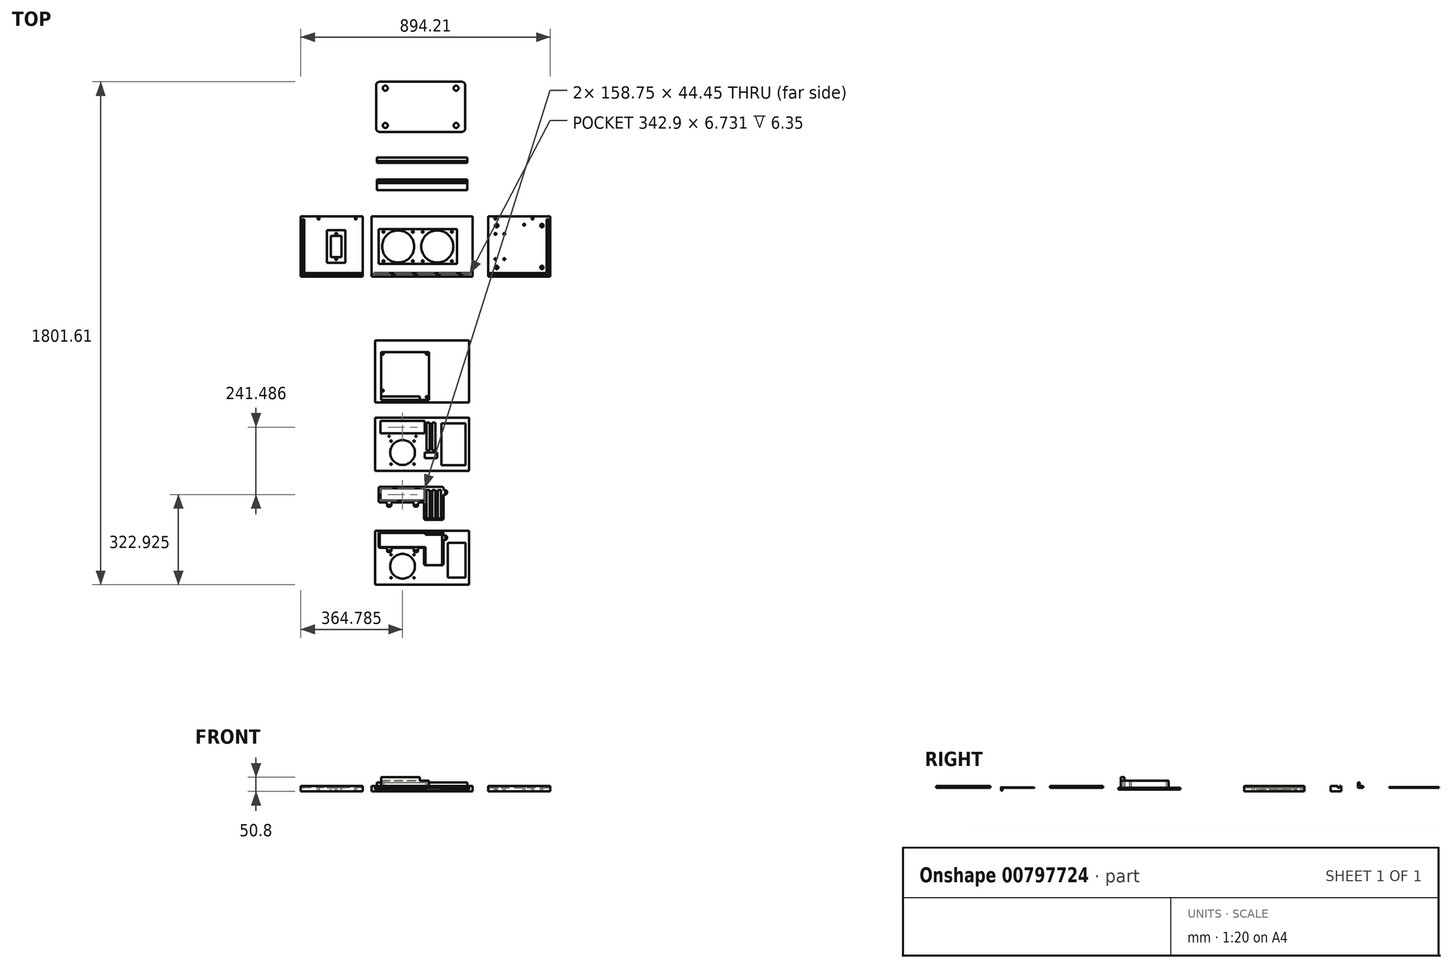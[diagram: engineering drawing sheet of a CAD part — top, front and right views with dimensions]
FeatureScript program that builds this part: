
annotation { "Feature Type Name" : "Feature", "Feature Type Description" : "" }
export const myFeature = defineFeature(function(context is Context, id is Id, definition is map)
    precondition{}
    {
        {
            var Q0;
            Q0=qCreatedBy(makeId("Top.planeOp"),FACE);
            var sketch = newSketch(context, id + "F0", { "sketchPlane" : qUnion([Q0])});
            skLineSegment(sketch, "E0.bottom", {"start": v(120.65, -107.95) * mm, "end": v(-241.3, -107.95) * mm});
            skLineSegment(sketch, "E0.top", {"start": v(120.65, 107.95) * mm, "end": v(-241.3, 107.95) * mm});
            skLineSegment(sketch, "E0.left", {"start": v(120.65, -107.95) * mm, "end": v(120.65, 107.95) * mm});
            skLineSegment(sketch, "E0.right", {"start": v(-241.3, -107.95) * mm, "end": v(-241.3, 107.95) * mm});
            skLineSegment(sketch, "E1.bottom", {"start": v(-231.77, -101.6) * mm, "end": v(111.12, -101.6) * mm});
            skLineSegment(sketch, "E1.top", {"start": v(-231.77, -94.87) * mm, "end": v(111.12, -94.87) * mm});
            skLineSegment(sketch, "E1.left", {"start": v(-231.77, -101.6) * mm, "end": v(-231.77, -94.87) * mm});
            skLineSegment(sketch, "E1.right", {"start": v(111.12, -101.6) * mm, "end": v(111.12, -94.87) * mm});
            skPoint(sketch, "E2.middle", {"position": v(-145.7, 0) * mm});
            skCircle(sketch, "E3", {"center": v(-145.7, 0) * mm, "radius": 57.5 * mm});
            skCircle(sketch, "E4", {"center": v(-198.2, 52.5) * mm, "radius": 3.3 * mm});
            skCircle(sketch, "E5", {"center": v(-93.2, 52.5) * mm, "radius": 3.3 * mm});
            skCircle(sketch, "E6", {"center": v(-198.2, -52.5) * mm, "radius": 3.3 * mm});
            skCircle(sketch, "E7", {"center": v(-93.2, -52.5) * mm, "radius": 3.3 * mm});
            skPoint(sketch, "E8.middle", {"position": v(-5.3, 0) * mm});
            skCircle(sketch, "E9", {"center": v(-5.3, 0) * mm, "radius": 57.5 * mm});
            skCircle(sketch, "E10", {"center": v(-57.8, 52.5) * mm, "radius": 3.3 * mm});
            skCircle(sketch, "E11", {"center": v(47.2, 52.5) * mm, "radius": 3.3 * mm});
            skCircle(sketch, "E12", {"center": v(-57.8, -52.5) * mm, "radius": 3.3 * mm});
            skCircle(sketch, "E13", {"center": v(47.2, -52.5) * mm, "radius": 3.3 * mm});
            skLineSegment(sketch, "E14.bottom", {"start": v(64.9, -62.5) * mm, "end": v(-215.9, -62.5) * mm});
            skLineSegment(sketch, "E14.top", {"start": v(64.9, 62.5) * mm, "end": v(-215.9, 62.5) * mm});
            skLineSegment(sketch, "E14.left", {"start": v(64.9, -62.5) * mm, "end": v(64.9, 62.5) * mm});
            skLineSegment(sketch, "E14.right", {"start": v(-215.9, -62.5) * mm, "end": v(-215.9, 62.5) * mm});
            skPoint(sketch, "E15", {"position": v(-60.33, 107.95) * mm});
            skSolve(sketch);
        }
        {
            var Q0;
            Q0=makeQuery(id+"F0.imprint","IMPRINT",FACE,{"disambiguationData":[TD([[makeQuery(id+"F0.imprint","IMPRINT",EDGE,{"derivedFrom":sQuery(id+"F0.wireOp",EDGE,"unbbHF4E-aeKD-aJLP-3i1E-MLkDgT7gMaSE.bottom")}),-1.0]])]});
            var Q1;
            Q1=makeQuery(id+"F0.imprint","IMPRINT",FACE,{"disambiguationData":[TD([[makeQuery(id+"F0.imprint","IMPRINT",EDGE,{"derivedFrom":sQuery(id+"F0.wireOp",EDGE,"E0.bottom")}),-1.0]])]});
            var Q2;
            Q2=makeQuery(id+"F0.imprint","IMPRINT",FACE,{"disambiguationData":[TD([[makeQuery(id+"F0.imprint","IMPRINT",EDGE,{"derivedFrom":sQuery(id+"F0.wireOp",EDGE,"DKvrWdsa-jCIU-vHXJ-xxZo-lPnyOnNzNnFu")}),-1.0]])]});
            var Q3;
            Q3=makeQuery(id+"F0.imprint","IMPRINT",FACE,{"disambiguationData":[TD([[makeQuery(id+"F0.imprint","IMPRINT",EDGE,{"derivedFrom":sQuery(id+"F0.wireOp",EDGE,"E1.bottom")}),1.0]])]});
            var Q4;
            Q4=makeQuery(id+"F0.imprint","IMPRINT",FACE,{"disambiguationData":[TD([[makeQuery(id+"F0.imprint","IMPRINT",EDGE,{"derivedFrom":sQuery(id+"F0.wireOp",EDGE,"E3")}),-1.0]])]});
            extrude(context, id + "F1", {"entities" : qUnion([Q0, Q1, Q2, Q3, Q4]), "oppositeDirection" : true, "depth" : 12.7 * mm, "offsetDistance" : 25.4 * mm});
        }
        {
            var Q0;
            Q0=makeQuery(id+"F0.imprint","IMPRINT",FACE,{"disambiguationData":[TD([[makeQuery(id+"F0.imprint","IMPRINT",EDGE,{"derivedFrom":sQuery(id+"F0.wireOp",EDGE,"E0.bottom")}),-1.0]])]});
            var Q1;
            Q1=makeQuery(id+"F0.imprint","IMPRINT",FACE,{"disambiguationData":[TD([[makeQuery(id+"F0.imprint","IMPRINT",EDGE,{"derivedFrom":sQuery(id+"F0.wireOp",EDGE,"E3")}),-1.0]])]});
            extrude(context, id + "F2", {"entities" : qUnion([Q0, Q1]), "operationType" : NewBodyOperationType.ADD, "depth" : 6.35 * mm, "offsetDistance" : 25.4 * mm});
        }
        {
            var Q0;
            Q0=qCreatedBy(makeId("Top.planeOp"),FACE);
            var sketch = newSketch(context, id + "F3", { "sketchPlane" : qUnion([Q0])});
            skPoint(sketch, "E16.2", {"position": v(120.65, -107.95) * mm});
            skPoint(sketch, "E16.3", {"position": v(120.65, 107.95) * mm});
            skLineSegment(sketch, "E17.bottom", {"start": v(177.35, -107.95) * mm, "end": v(399.6, -107.95) * mm});
            skLineSegment(sketch, "E17.top", {"start": v(177.35, 107.95) * mm, "end": v(399.6, 107.95) * mm});
            skLineSegment(sketch, "E17.left", {"start": v(177.35, -107.95) * mm, "end": v(177.35, 107.95) * mm});
            skLineSegment(sketch, "E17.right", {"start": v(399.6, -107.95) * mm, "end": v(399.6, 107.95) * mm});
            skPoint(sketch, "E17.middle", {"position": v(288.48, 0) * mm});
            skLineSegment(sketch, "E18.bottom", {"start": v(174.18, -94.87) * mm, "end": v(393.25, -94.87) * mm});
            skLineSegment(sketch, "E18.top", {"start": v(174.18, -101.6) * mm, "end": v(393.25, -101.6) * mm});
            skLineSegment(sketch, "E18.left", {"start": v(174.18, -94.87) * mm, "end": v(174.18, -101.6) * mm});
            skLineSegment(sketch, "E18.right", {"start": v(393.25, -94.87) * mm, "end": v(393.25, -101.6) * mm});
            skLineSegment(sketch, "E19.bottom", {"start": v(393.25, -98.42) * mm, "end": v(386.52, -98.42) * mm});
            skLineSegment(sketch, "E19.top", {"start": v(393.25, 98.42) * mm, "end": v(386.52, 98.42) * mm});
            skLineSegment(sketch, "E19.left", {"start": v(393.25, -98.42) * mm, "end": v(393.25, 98.43) * mm});
            skLineSegment(sketch, "E19.right", {"start": v(386.52, -98.42) * mm, "end": v(386.52, 98.42) * mm});
            skCircle(sketch, "E20", {"center": v(207.35, 74.95) * mm, "radius": 3.3 * mm});
            skCircle(sketch, "E21", {"center": v(207.35, -74.95) * mm, "radius": 3.3 * mm});
            skCircle(sketch, "E22", {"center": v(369.6, -74.95) * mm, "radius": 3.3 * mm});
            skCircle(sketch, "E23", {"center": v(369.6, 74.95) * mm, "radius": 3.3 * mm});
            skCircle(sketch, "E24", {"center": v(207.35, 74.95) * mm, "radius": 6 * mm});
            skCircle(sketch, "E25", {"center": v(207.35, -74.95) * mm, "radius": 6 * mm});
            skCircle(sketch, "E26", {"center": v(369.6, 74.95) * mm, "radius": 6 * mm});
            skCircle(sketch, "E27", {"center": v(369.6, -74.95) * mm, "radius": 6 * mm});
            skPoint(sketch, "E28", {"position": v(298, -20.34) * mm});
            skCircle(sketch, "E29", {"center": v(335.9, 99.95) * mm, "radius": 3.3 * mm});
            skCircle(sketch, "E30", {"center": v(202.75, 99.95) * mm, "radius": 3.3 * mm});
            skPoint(sketch, "E31.centerSnap0", {"position": v(177.35, 0) * mm});
            skCircle(sketch, "E32", {"center": v(306.02, 78.45) * mm, "radius": 3.3 * mm});
            skLineSegment(sketch, "E33.bottom", {"start": v(234.55, -45.09) * mm, "end": v(202.75, -45.09) * mm});
            skLineSegment(sketch, "E33.top", {"start": v(234.55, 45.08) * mm, "end": v(202.75, 45.08) * mm});
            skLineSegment(sketch, "E33.left", {"start": v(234.55, -45.09) * mm, "end": v(234.55, 45.08) * mm});
            skLineSegment(sketch, "E33.right", {"start": v(202.75, -45.09) * mm, "end": v(202.75, 45.08) * mm});
            skPoint(sketch, "E33.middle", {"position": v(218.65, 0) * mm});
            skCircle(sketch, "E34", {"center": v(202.75, 45.08) * mm, "radius": 3.3 * mm});
            skCircle(sketch, "E35", {"center": v(234.55, 45.08) * mm, "radius": 3.3 * mm});
            skCircle(sketch, "E36", {"center": v(202.75, -45.09) * mm, "radius": 3.3 * mm});
            skCircle(sketch, "E37", {"center": v(234.55, -45.09) * mm, "radius": 3.3 * mm});
            skPoint(sketch, "E38.0", {"position": v(111.12, -94.87) * mm});
            skPoint(sketch, "E38.1", {"position": v(111.12, -101.6) * mm});
            skSolve(sketch);
        }
        {
            var Q0;
            {var subQ0=sQuery(id+"F3.wireOp",EDGE,"E17.left");var subQ1=sQuery(id+"F3.wireOp",EDGE,"E17.top");var subQ2=makeQuery(id+"F3.imprint","INTERSECT",VERTEX,{"derivedFrom":[subQ1,subQ0]});Q0=makeQuery(id+"F3.imprint","IMPRINT",FACE,{"disambiguationData":[TD([[makeQuery(id+"F3.imprint","IMPRINT",EDGE,{"disambiguationData":[TD([[subQ2,-1.0]])],"derivedFrom":subQ1}),-1.0]])]});}
            var Q1;
            {var subQ0=sQuery(id+"F3.wireOp",EDGE,"E19.right");var subQ1=sQuery(id+"F3.wireOp",EDGE,"E17.top");var subQ2=makeQuery(id+"F3.imprint","INTERSECT",VERTEX,{"derivedFrom":[subQ1,subQ0]});Q1=makeQuery(id+"F3.imprint","IMPRINT",FACE,{"disambiguationData":[TD([[makeQuery(id+"F3.imprint","IMPRINT",EDGE,{"disambiguationData":[TD([[subQ2,-1.0]])],"derivedFrom":subQ1}),-1.0]])]});}
            var Q2;
            {var subQ0=sQuery(id+"F3.wireOp",EDGE,"E17.right");var subQ1=sQuery(id+"F3.wireOp",EDGE,"E17.top");var subQ2=makeQuery(id+"F3.imprint","INTERSECT",VERTEX,{"derivedFrom":[subQ1,subQ0]});Q2=makeQuery(id+"F3.imprint","IMPRINT",FACE,{"disambiguationData":[TD([[makeQuery(id+"F3.imprint","IMPRINT",EDGE,{"disambiguationData":[TD([[subQ2,1.0]])],"derivedFrom":subQ1}),-1.0]])]});}
            var Q3;
            {var subQ6=sQuery(id+"F3.wireOp",EDGE,"E19.bottom");Q3=makeQuery(id+"F3.imprint","IMPRINT",FACE,{"disambiguationData":[TD([[makeQuery(id+"F3.imprint","IMPRINT",EDGE,{"derivedFrom":subQ6}),1.0]])]});}
            var Q4;
            {var subQ0=sQuery(id+"F3.wireOp",EDGE,"E17.bottom");Q4=makeQuery(id+"F3.imprint","IMPRINT",FACE,{"disambiguationData":[TD([[makeQuery(id+"F3.imprint","IMPRINT",EDGE,{"derivedFrom":subQ0}),1.0]])]});}
            var Q5;
            {var subQ5=sQuery(id+"F3.wireOp",EDGE,"E19.bottom");Q5=makeQuery(id+"F3.imprint","IMPRINT",FACE,{"disambiguationData":[TD([[makeQuery(id+"F3.imprint","IMPRINT",EDGE,{"derivedFrom":subQ5}),-1.0]])]});}
            var Q6;
            {var subQ5=sQuery(id+"F3.wireOp",EDGE,"E19.top");Q6=makeQuery(id+"F3.imprint","IMPRINT",FACE,{"disambiguationData":[TD([[makeQuery(id+"F3.imprint","IMPRINT",EDGE,{"derivedFrom":subQ5}),1.0]])]});}
            var Q7;
            Q7=makeQuery(id+"F3.imprint","IMPRINT",FACE,{"disambiguationData":[TD([[makeQuery(id+"F3.imprint","IMPRINT",EDGE,{"derivedFrom":sQuery(id+"F3.wireOp",EDGE,"E20")}),-1.0]])]});
            var Q8;
            Q8=makeQuery(id+"F3.imprint","IMPRINT",FACE,{"disambiguationData":[TD([[makeQuery(id+"F3.imprint","IMPRINT",EDGE,{"derivedFrom":sQuery(id+"F3.wireOp",EDGE,"E21")}),-1.0]])]});
            var Q9;
            Q9=makeQuery(id+"F3.imprint","IMPRINT",FACE,{"disambiguationData":[TD([[makeQuery(id+"F3.imprint","IMPRINT",EDGE,{"derivedFrom":sQuery(id+"F3.wireOp",EDGE,"E22")}),-1.0]])]});
            var Q10;
            Q10=makeQuery(id+"F3.imprint","IMPRINT",FACE,{"disambiguationData":[TD([[makeQuery(id+"F3.imprint","IMPRINT",EDGE,{"derivedFrom":sQuery(id+"F3.wireOp",EDGE,"E23")}),-1.0]])]});
            var Q11;
            {var subQ0=sQuery(id+"F3.wireOp",EDGE,"E33.top");var subQ1=sQuery(id+"F3.wireOp",EDGE,"oCOWhfAx-kF6R-myvc-yPfL-ItVIfWdrZVwj");var subQ2=makeQuery(id+"F3.imprint","INTERSECT",VERTEX,{"derivedFrom":[subQ1,subQ0]});Q11=makeQuery(id+"F3.imprint","IMPRINT",FACE,{"disambiguationData":[TD([[makeQuery(id+"F3.imprint","IMPRINT",EDGE,{"disambiguationData":[TD([[subQ2,-1.0]])],"derivedFrom":subQ1}),-1.0]])]});}
            var Q12;
            {var subQ5=sQuery(id+"F3.wireOp",EDGE,"E33.top");var subQ6=sQuery(id+"F3.wireOp",EDGE,"oCOWhfAx-kF6R-myvc-yPfL-ItVIfWdrZVwj");var subQ7=makeQuery(id+"F3.imprint","INTERSECT",VERTEX,{"derivedFrom":[subQ6,subQ5]});Q12=makeQuery(id+"F3.imprint","IMPRINT",FACE,{"disambiguationData":[TD([[makeQuery(id+"F3.imprint","IMPRINT",EDGE,{"disambiguationData":[TD([[subQ7,-1.0]])],"derivedFrom":subQ6}),1.0]])]});}
            var Q13;
            {var subQ5=sQuery(id+"F3.wireOp",EDGE,"E37");var subQ10=sQuery(id+"F3.wireOp",EDGE,"E33.bottom");var subQ11=makeQuery(id+"F3.imprint","INTERSECT",VERTEX,{"derivedFrom":[subQ10,subQ5]});Q13=makeQuery(id+"F3.imprint","IMPRINT",FACE,{"disambiguationData":[TD([[makeQuery(id+"F3.imprint","IMPRINT",EDGE,{"disambiguationData":[TD([[subQ11,-1.0]])],"derivedFrom":subQ10}),-1.0]])]});}
            extrude(context, id + "F4", {"entities" : qUnion([Q0, Q1, Q2, Q3, Q4, Q5, Q6, Q7, Q8, Q9, Q10, Q11, Q12, Q13]), "oppositeDirection" : true, "depth" : 12.7 * mm, "offsetDistance" : 25.4 * mm});
        }
        {
            var Q0;
            {var subQ0=sQuery(id+"F3.wireOp",EDGE,"E17.left");var subQ1=sQuery(id+"F3.wireOp",EDGE,"E17.top");var subQ2=makeQuery(id+"F3.imprint","INTERSECT",VERTEX,{"derivedFrom":[subQ1,subQ0]});Q0=makeQuery(id+"F3.imprint","IMPRINT",FACE,{"disambiguationData":[TD([[makeQuery(id+"F3.imprint","IMPRINT",EDGE,{"disambiguationData":[TD([[subQ2,-1.0]])],"derivedFrom":subQ1}),-1.0]])]});}
            var Q1;
            {var subQ0=sQuery(id+"F3.wireOp",EDGE,"E17.right");var subQ1=sQuery(id+"F3.wireOp",EDGE,"E17.top");var subQ2=makeQuery(id+"F3.imprint","INTERSECT",VERTEX,{"derivedFrom":[subQ1,subQ0]});Q1=makeQuery(id+"F3.imprint","IMPRINT",FACE,{"disambiguationData":[TD([[makeQuery(id+"F3.imprint","IMPRINT",EDGE,{"disambiguationData":[TD([[subQ2,1.0]])],"derivedFrom":subQ1}),-1.0]])]});}
            var Q2;
            {var subQ0=sQuery(id+"F3.wireOp",EDGE,"E17.bottom");Q2=makeQuery(id+"F3.imprint","IMPRINT",FACE,{"disambiguationData":[TD([[makeQuery(id+"F3.imprint","IMPRINT",EDGE,{"derivedFrom":subQ0}),1.0]])]});}
            var Q3;
            {var subQ0=sQuery(id+"F3.wireOp",EDGE,"E33.top");var subQ1=sQuery(id+"F3.wireOp",EDGE,"oCOWhfAx-kF6R-myvc-yPfL-ItVIfWdrZVwj");var subQ2=makeQuery(id+"F3.imprint","INTERSECT",VERTEX,{"derivedFrom":[subQ1,subQ0]});Q3=makeQuery(id+"F3.imprint","IMPRINT",FACE,{"disambiguationData":[TD([[makeQuery(id+"F3.imprint","IMPRINT",EDGE,{"disambiguationData":[TD([[subQ2,-1.0]])],"derivedFrom":subQ1}),-1.0]])]});}
            var Q4;
            {var subQ5=sQuery(id+"F3.wireOp",EDGE,"E33.top");var subQ6=sQuery(id+"F3.wireOp",EDGE,"oCOWhfAx-kF6R-myvc-yPfL-ItVIfWdrZVwj");var subQ7=makeQuery(id+"F3.imprint","INTERSECT",VERTEX,{"derivedFrom":[subQ6,subQ5]});Q4=makeQuery(id+"F3.imprint","IMPRINT",FACE,{"disambiguationData":[TD([[makeQuery(id+"F3.imprint","IMPRINT",EDGE,{"disambiguationData":[TD([[subQ7,-1.0]])],"derivedFrom":subQ6}),1.0]])]});}
            var Q5;
            {var subQ5=sQuery(id+"F3.wireOp",EDGE,"E37");var subQ10=sQuery(id+"F3.wireOp",EDGE,"E33.bottom");var subQ11=makeQuery(id+"F3.imprint","INTERSECT",VERTEX,{"derivedFrom":[subQ10,subQ5]});Q5=makeQuery(id+"F3.imprint","IMPRINT",FACE,{"disambiguationData":[TD([[makeQuery(id+"F3.imprint","IMPRINT",EDGE,{"disambiguationData":[TD([[subQ11,-1.0]])],"derivedFrom":subQ10}),-1.0]])]});}
            extrude(context, id + "F5", {"entities" : qUnion([Q0, Q1, Q2, Q3, Q4, Q5]), "operationType" : NewBodyOperationType.ADD, "depth" : 6.35 * mm, "offsetDistance" : 25.4 * mm});
        }
        {
            var Q0;
            Q0=qCreatedBy(makeId("Top.planeOp"),FACE);
            var sketch = newSketch(context, id + "F6", { "sketchPlane" : qUnion([Q0])});
            skPoint(sketch, "E39.0", {"position": v(-241.3, 107.95) * mm});
            skPoint(sketch, "E39.1", {"position": v(-241.3, -107.95) * mm});
            skPoint(sketch, "E39.2", {"position": v(-269.24, -94.87) * mm});
            skPoint(sketch, "E39.3", {"position": v(-269.24, -101.6) * mm});
            skLineSegment(sketch, "E40.bottom", {"start": v(-272.36, 107.95) * mm, "end": v(-494.6, 107.95) * mm});
            skLineSegment(sketch, "E40.top", {"start": v(-272.36, -107.95) * mm, "end": v(-494.6, -107.95) * mm});
            skLineSegment(sketch, "E40.left", {"start": v(-272.36, 107.95) * mm, "end": v(-272.36, -107.95) * mm});
            skLineSegment(sketch, "E40.right", {"start": v(-494.6, 107.95) * mm, "end": v(-494.6, -107.95) * mm});
            skLineSegment(sketch, "E41.bottom", {"start": v(-269.18, -94.87) * mm, "end": v(-488.26, -94.87) * mm});
            skLineSegment(sketch, "E41.top", {"start": v(-269.18, -101.6) * mm, "end": v(-488.26, -101.6) * mm});
            skLineSegment(sketch, "E41.left", {"start": v(-269.18, -94.87) * mm, "end": v(-269.18, -101.6) * mm});
            skLineSegment(sketch, "E41.right", {"start": v(-488.26, -94.87) * mm, "end": v(-488.26, -101.6) * mm});
            skLineSegment(sketch, "E42.bottom", {"start": v(-348.56, -38.1) * mm, "end": v(-386.66, -38.1) * mm});
            skLineSegment(sketch, "E42.top", {"start": v(-348.56, 38.1) * mm, "end": v(-386.66, 38.1) * mm});
            skLineSegment(sketch, "E42.left", {"start": v(-348.56, -38.1) * mm, "end": v(-348.56, 38.1) * mm});
            skLineSegment(sketch, "E42.right", {"start": v(-386.66, -38.1) * mm, "end": v(-386.66, 38.1) * mm});
            skPoint(sketch, "E42.middle", {"position": v(-367.6, 0) * mm});
            skLineSegment(sketch, "E43.bottom", {"start": v(-488.26, 98.42) * mm, "end": v(-481.53, 98.42) * mm});
            skLineSegment(sketch, "E43.top", {"start": v(-488.26, -98.43) * mm, "end": v(-481.53, -98.43) * mm});
            skLineSegment(sketch, "E43.left", {"start": v(-488.26, 98.42) * mm, "end": v(-488.26, -98.43) * mm});
            skLineSegment(sketch, "E43.right", {"start": v(-481.53, 98.43) * mm, "end": v(-481.53, -98.43) * mm});
            skPoint(sketch, "E44.0", {"position": v(202.75, 99.95) * mm});
            skCircle(sketch, "E45", {"center": v(-297.76, 99.95) * mm, "radius": 3.3 * mm});
            skCircle(sketch, "E46", {"center": v(-430.9, 99.95) * mm, "radius": 3.3 * mm});
            skCircle(sketch, "E47", {"center": v(-367.6, 45.6) * mm, "radius": 3.3 * mm});
            skCircle(sketch, "E48", {"center": v(-367.6, -45.6) * mm, "radius": 3.3 * mm});
            skLineSegment(sketch, "E49.bottom", {"start": v(-400.63, 58.42) * mm, "end": v(-334.59, 58.42) * mm});
            skLineSegment(sketch, "E49.top", {"start": v(-400.63, -58.42) * mm, "end": v(-334.59, -58.42) * mm});
            skLineSegment(sketch, "E49.left", {"start": v(-400.63, 58.42) * mm, "end": v(-400.63, -58.42) * mm});
            skLineSegment(sketch, "E49.right", {"start": v(-334.59, 58.42) * mm, "end": v(-334.59, -58.42) * mm});
            skPoint(sketch, "E50.0", {"position": v(-231.77, -94.87) * mm});
            skPoint(sketch, "E50.1", {"position": v(-231.77, -101.6) * mm});
            skSolve(sketch);
        }
        {
            var Q0;
            Q0=makeQuery(id+"F6.imprint","IMPRINT",FACE,{"disambiguationData":[TD([[makeQuery(id+"F6.imprint","IMPRINT",EDGE,{"derivedFrom":sQuery(id+"F6.wireOp",EDGE,"E42.bottom")}),1.0]])]});
            var Q1;
            {var subQ0=sQuery(id+"F6.wireOp",EDGE,"E40.top");Q1=makeQuery(id+"F6.imprint","IMPRINT",FACE,{"disambiguationData":[TD([[makeQuery(id+"F6.imprint","IMPRINT",EDGE,{"derivedFrom":subQ0}),-1.0]])]});}
            var Q2;
            {var subQ12=sQuery(id+"F6.wireOp",EDGE,"E43.top");Q2=makeQuery(id+"F6.imprint","IMPRINT",FACE,{"disambiguationData":[TD([[makeQuery(id+"F6.imprint","IMPRINT",EDGE,{"derivedFrom":subQ12}),-1.0]])]});}
            var Q3;
            {var subQ0=sQuery(id+"F6.wireOp",EDGE,"E40.right");var subQ1=sQuery(id+"F6.wireOp",EDGE,"E40.bottom");var subQ2=makeQuery(id+"F6.imprint","INTERSECT",VERTEX,{"derivedFrom":[subQ1,subQ0]});Q3=makeQuery(id+"F6.imprint","IMPRINT",FACE,{"disambiguationData":[TD([[makeQuery(id+"F6.imprint","IMPRINT",EDGE,{"disambiguationData":[TD([[subQ2,1.0]])],"derivedFrom":subQ1}),1.0]])]});}
            var Q4;
            {var subQ0=sQuery(id+"F6.wireOp",EDGE,"E43.right");var subQ1=sQuery(id+"F6.wireOp",EDGE,"E40.bottom");var subQ2=makeQuery(id+"F6.imprint","INTERSECT",VERTEX,{"derivedFrom":[subQ1,subQ0]});Q4=makeQuery(id+"F6.imprint","IMPRINT",FACE,{"disambiguationData":[TD([[makeQuery(id+"F6.imprint","IMPRINT",EDGE,{"disambiguationData":[TD([[subQ2,-1.0]])],"derivedFrom":subQ1}),1.0]])]});}
            var Q5;
            {var subQ5=sQuery(id+"F6.wireOp",EDGE,"E43.top");Q5=makeQuery(id+"F6.imprint","IMPRINT",FACE,{"disambiguationData":[TD([[makeQuery(id+"F6.imprint","IMPRINT",EDGE,{"derivedFrom":subQ5}),1.0]])]});}
            var Q6;
            {var subQ5=sQuery(id+"F6.wireOp",EDGE,"E43.bottom");Q6=makeQuery(id+"F6.imprint","IMPRINT",FACE,{"disambiguationData":[TD([[makeQuery(id+"F6.imprint","IMPRINT",EDGE,{"derivedFrom":subQ5}),-1.0]])]});}
            extrude(context, id + "F7", {"entities" : qUnion([Q0, Q1, Q2, Q3, Q4, Q5, Q6]), "oppositeDirection" : true, "depth" : 12.7 * mm, "offsetDistance" : 25.4 * mm});
        }
        {
            var Q0;
            Q0=makeQuery(id+"F6.imprint","IMPRINT",FACE,{"disambiguationData":[TD([[makeQuery(id+"F6.imprint","IMPRINT",EDGE,{"derivedFrom":sQuery(id+"F6.wireOp",EDGE,"E42.bottom")}),1.0]])]});
            var Q1;
            {var subQ0=sQuery(id+"F6.wireOp",EDGE,"E40.right");var subQ1=sQuery(id+"F6.wireOp",EDGE,"E40.bottom");var subQ2=makeQuery(id+"F6.imprint","INTERSECT",VERTEX,{"derivedFrom":[subQ1,subQ0]});Q1=makeQuery(id+"F6.imprint","IMPRINT",FACE,{"disambiguationData":[TD([[makeQuery(id+"F6.imprint","IMPRINT",EDGE,{"disambiguationData":[TD([[subQ2,1.0]])],"derivedFrom":subQ1}),1.0]])]});}
            var Q2;
            {var subQ0=sQuery(id+"F6.wireOp",EDGE,"E40.top");Q2=makeQuery(id+"F6.imprint","IMPRINT",FACE,{"disambiguationData":[TD([[makeQuery(id+"F6.imprint","IMPRINT",EDGE,{"derivedFrom":subQ0}),-1.0]])]});}
            extrude(context, id + "F8", {"entities" : qUnion([Q0, Q1, Q2]), "operationType" : NewBodyOperationType.ADD, "depth" : 6.35 * mm, "offsetDistance" : 25.4 * mm});
        }
        {
            var Q0;
            Q0=makeQuery(id+"F6.imprint","IMPRINT",FACE,{"disambiguationData":[TD([[makeQuery(id+"F6.imprint","IMPRINT",EDGE,{"derivedFrom":sQuery(id+"F6.wireOp",EDGE,"E42.bottom")}),1.0]])]});
            extrude(context, id + "F9", {"entities" : qUnion([Q0]), "operationType" : NewBodyOperationType.REMOVE, "depth" : 6.35 * mm, "offsetDistance" : 25.4 * mm});
        }
        {
            var Q0;
            Q0=qCreatedBy(makeId("Top.planeOp"),FACE);
            var sketch = newSketch(context, id + "F10", { "sketchPlane" : qUnion([Q0])});
            skLineSegment(sketch, "E51.bottom", {"start": v(-35.35, -378) * mm, "end": v(-35.35, -549.45) * mm});
            skLineSegment(sketch, "E51.top", {"start": v(-206.8, -378) * mm, "end": v(-206.8, -549.45) * mm});
            skLineSegment(sketch, "E51.left", {"start": v(-35.35, -378) * mm, "end": v(-206.8, -378) * mm});
            skLineSegment(sketch, "E51.right", {"start": v(-35.35, -549.45) * mm, "end": v(-206.8, -549.45) * mm});
            skLineSegment(sketch, "E52.bottom", {"start": v(-68.71, -549.45) * mm, "end": v(-68.71, -536.83) * mm});
            skLineSegment(sketch, "E52.top", {"start": v(-206.8, -549.45) * mm, "end": v(-206.8, -536.83) * mm});
            skLineSegment(sketch, "E52.left", {"start": v(-68.71, -549.45) * mm, "end": v(-206.8, -549.45) * mm});
            skLineSegment(sketch, "E52.right", {"start": v(-68.71, -536.83) * mm, "end": v(-206.8, -536.83) * mm});
            skCircle(sketch, "E53", {"center": v(-42.97, -539.29) * mm, "radius": 3.3 * mm});
            skCircle(sketch, "E54", {"center": v(-42.97, -384.35) * mm, "radius": 3.3 * mm});
            skCircle(sketch, "E55", {"center": v(-200.45, -384.35) * mm, "radius": 3.3 * mm});
            skCircle(sketch, "E56", {"center": v(-200.45, -516.43) * mm, "radius": 3.3 * mm});
            skSolve(sketch);
        }
        {
            var Q0;
            {var subQ4=sQuery(id+"F10.wireOp",EDGE,"E51.bottom");Q0=makeQuery(id+"F10.imprint","IMPRINT",FACE,{"disambiguationData":[TD([[makeQuery(id+"F10.imprint","IMPRINT",EDGE,{"derivedFrom":subQ4}),-1.0]])]});}
            var Q1;
            {var subQ4=sQuery(id+"F10.wireOp",EDGE,"E52.bottom");Q1=makeQuery(id+"F10.imprint","IMPRINT",FACE,{"disambiguationData":[TD([[makeQuery(id+"F10.imprint","IMPRINT",EDGE,{"derivedFrom":subQ4}),1.0]])]});}
            extrude(context, id + "F11", {"entities" : qUnion([Q0, Q1]), "depth" : 25.4 * mm, "offsetDistance" : 25.4 * mm});
        }
        {
            var Q0;
            {var subQ4=sQuery(id+"F10.wireOp",EDGE,"E52.bottom");Q0=makeQuery(id+"F10.imprint","IMPRINT",FACE,{"disambiguationData":[TD([[makeQuery(id+"F10.imprint","IMPRINT",EDGE,{"derivedFrom":subQ4}),1.0]])]});}
            extrude(context, id + "F12", {"entities" : qUnion([Q0]), "operationType" : NewBodyOperationType.ADD, "depth" : 38.1 * mm, "offsetDistance" : 25.4 * mm});
        }
        {
            var Q0;
            Q0=qCreatedBy(makeId("Top.planeOp"),FACE);
            var sketch = newSketch(context, id + "F13", { "sketchPlane" : qUnion([Q0])});
            skLineSegment(sketch, "E57.top", {"start": v(107.95, -336.22) * mm, "end": v(-228.6, -336.22) * mm});
            skPoint(sketch, "E58.0", {"position": v(-241.3, -107.95) * mm});
            skPoint(sketch, "E58.1", {"position": v(120.65, -107.95) * mm});
            skCircle(sketch, "E59.8", {"center": v(-42.97, -384.35) * mm, "radius": 3.3 * mm});
            skPoint(sketch, "E59.9", {"position": v(-42.97, -384.35) * mm});
            skCircle(sketch, "E59.10", {"center": v(-200.45, -384.35) * mm, "radius": 3.3 * mm});
            skPoint(sketch, "E59.11", {"position": v(-200.45, -384.35) * mm});
            skCircle(sketch, "E59.12", {"center": v(-200.45, -516.43) * mm, "radius": 3.3 * mm});
            skPoint(sketch, "E59.13", {"position": v(-200.45, -516.43) * mm});
            skCircle(sketch, "E59.14", {"center": v(-42.97, -539.29) * mm, "radius": 3.3 * mm});
            skPoint(sketch, "E59.15", {"position": v(-42.97, -539.29) * mm});
            skLineSegment(sketch, "E60", {"start": v(107.95, -336.22) * mm, "end": v(107.95, -558.47) * mm});
            skLineSegment(sketch, "E61", {"start": v(-228.6, -336.22) * mm, "end": v(-228.6, -551.95) * mm});
            skLineSegment(sketch, "E62", {"start": v(-228.6, -551.95) * mm, "end": v(-228.6, -558.47) * mm});
            skLineSegment(sketch, "E63", {"start": v(-228.6, -558.47) * mm, "end": v(107.95, -558.47) * mm});
            skSolve(sketch);
        }
        {
            var Q0;
            {var subQ0=sQuery(id+"F13.wireOp",EDGE,"E57.top");Q0=makeQuery(id+"F13.imprint","IMPRINT",FACE,{"disambiguationData":[TD([[makeQuery(id+"F13.imprint","IMPRINT",EDGE,{"derivedFrom":subQ0}),1.0]])]});}
            var Q1;
            {var subQ0=sQuery(id+"F13.wireOp",EDGE,"zqHJPGBF-RlaW-aas7-9g15-NJBOEXlx8RhR.bottom");var subQ1=sQuery(id+"F13.wireOp",EDGE,"E57.left");var subQ2=makeQuery(id+"F13.imprint","INTERSECT",VERTEX,{"derivedFrom":[subQ1,subQ0]});Q1=makeQuery(id+"F13.imprint","IMPRINT",FACE,{"disambiguationData":[TD([[makeQuery(id+"F13.imprint","IMPRINT",EDGE,{"disambiguationData":[TD([[subQ2,-1.0]])],"derivedFrom":subQ1}),1.0]])]});}
            var Q2;
            {var subQ0=sQuery(id+"F13.wireOp",EDGE,"E57.bottom");Q2=makeQuery(id+"F13.imprint","IMPRINT",FACE,{"disambiguationData":[TD([[makeQuery(id+"F13.imprint","IMPRINT",EDGE,{"derivedFrom":subQ0}),-1.0]])]});}
            var Q3;
            {var subQ3=sQuery(id+"F13.wireOp",EDGE,"E62");Q3=makeQuery(id+"F13.imprint","IMPRINT",FACE,{"disambiguationData":[TD([[makeQuery(id+"F13.imprint","IMPRINT",EDGE,{"derivedFrom":subQ3}),1.0]])]});}
            extrude(context, id + "F14", {"entities" : qUnion([Q0, Q1, Q2, Q3]), "oppositeDirection" : true, "depth" : 6.4 * mm, "offsetDistance" : 25.4 * mm});
        }
        {
            var Q0;
            Q0=qCreatedBy(makeId("Top.planeOp"),FACE);
            var sketch = newSketch(context, id + "F15", { "sketchPlane" : qUnion([Q0])});
            skLineSegment(sketch, "E64.MirrorCS", {"start": v(-11.95, -630.96) * mm, "end": v(-23.95, -630.96) * mm});
            skLineSegment(sketch, "E65.MirrorCS", {"start": v(-32.45, -730.34) * mm, "end": v(-44.45, -730.34) * mm});
            skLineSegment(sketch, "E66.MirrorCS", {"start": v(-11.95, -730.34) * mm, "end": v(-23.95, -730.34) * mm});
            skLineSegment(sketch, "E67.MirrorCS", {"start": v(-32.45, -630.96) * mm, "end": v(-44.45, -630.96) * mm});
            skLineSegment(sketch, "E68.MirrorCS", {"start": v(-50.8, -737.96) * mm, "end": v(-50.8, -757.96) * mm});
            skLineSegment(sketch, "E69.MirrorCS", {"start": v(-50.8, -737.96) * mm, "end": v(-5.6, -737.96) * mm});
            skLineSegment(sketch, "E70.MirrorCS", {"start": v(-5.6, -737.96) * mm, "end": v(-5.6, -757.96) * mm});
            skLineSegment(sketch, "E71.MirrorCS", {"start": v(-11.95, -730.34) * mm, "end": v(-11.95, -630.96) * mm});
            skLineSegment(sketch, "E72.MirrorCS", {"start": v(-5.6, -757.96) * mm, "end": v(-50.8, -757.96) * mm});
            skLineSegment(sketch, "E73.MirrorCS", {"start": v(-32.45, -730.34) * mm, "end": v(-32.45, -630.96) * mm});
            skLineSegment(sketch, "E74.MirrorCS", {"start": v(107.95, -804.15) * mm, "end": v(107.95, -613.76) * mm});
            skLineSegment(sketch, "E75.MirrorCS", {"start": v(-228.6, -804.15) * mm, "end": v(-228.6, -613.76) * mm});
            skLineSegment(sketch, "E76.MirrorCS", {"start": v(107.95, -804.15) * mm, "end": v(-228.6, -804.15) * mm});
            skLineSegment(sketch, "E77.MirrorCS", {"start": v(107.95, -613.76) * mm, "end": v(-228.6, -613.76) * mm});
            skLineSegment(sketch, "E78.MirrorCS", {"start": v(-23.95, -730.34) * mm, "end": v(-23.95, -630.96) * mm});
            skLineSegment(sketch, "E79.MirrorCS", {"start": v(-44.45, -730.34) * mm, "end": v(-44.45, -630.96) * mm});
            skLineSegment(sketch, "E80.bottom", {"start": v(-209.2, -624.96) * mm, "end": v(-50.45, -624.96) * mm});
            skLineSegment(sketch, "E80.top", {"start": v(-209.2, -669.41) * mm, "end": v(-50.45, -669.41) * mm});
            skLineSegment(sketch, "E80.left", {"start": v(-209.2, -624.96) * mm, "end": v(-209.2, -669.41) * mm});
            skLineSegment(sketch, "E80.right", {"start": v(-50.45, -624.96) * mm, "end": v(-50.45, -669.41) * mm});
            skPoint(sketch, "E81.middle.positionSnap0", {"position": v(107.95, -708.96) * mm});
            skPoint(sketch, "E81.centerSnap0", {"position": v(107.95, -708.96) * mm});
            skCircle(sketch, "E82", {"center": v(-129.82, -738.1) * mm, "radius": 44.5 * mm});
            skCircle(sketch, "E83", {"center": v(-171.07, -696.86) * mm, "radius": 2.5 * mm});
            skCircle(sketch, "E84", {"center": v(-88.57, -696.86) * mm, "radius": 2.5 * mm});
            skCircle(sketch, "E85", {"center": v(-171.07, -779.36) * mm, "radius": 2.5 * mm});
            skCircle(sketch, "E86", {"center": v(-88.57, -779.36) * mm, "radius": 2.5 * mm});
            skCircle(sketch, "E87", {"center": v(-177.93, -679.91) * mm, "radius": 2.1 * mm});
            skCircle(sketch, "E88", {"center": v(-81.73, -679.91) * mm, "radius": 2.18 * mm});
            skLineSegment(sketch, "E89.bottom", {"start": v(95.25, -783.96) * mm, "end": v(9.25, -783.96) * mm});
            skLineSegment(sketch, "E89.top", {"start": v(95.25, -633.96) * mm, "end": v(9.25, -633.96) * mm});
            skLineSegment(sketch, "E89.left", {"start": v(95.25, -783.96) * mm, "end": v(95.25, -633.96) * mm});
            skLineSegment(sketch, "E89.right", {"start": v(9.25, -783.96) * mm, "end": v(9.25, -633.96) * mm});
            skPoint(sketch, "E89.middle", {"position": v(52.25, -708.96) * mm});
            skSolve(sketch);
        }
        {
            var Q0;
            Q0=makeQuery(id+"F15.imprint","IMPRINT",FACE,{"disambiguationData":[TD([[makeQuery(id+"F15.imprint","IMPRINT",EDGE,{"derivedFrom":sQuery(id+"F15.wireOp",EDGE,"18db0fc0-b0b0-4d6d-8600-12bb63c691c31.MirrorCS")}),-1.0]])]});
            var Q1;
            Q1=makeQuery(id+"F15.imprint","IMPRINT",FACE,{"disambiguationData":[TD([[makeQuery(id+"F15.imprint","IMPRINT",EDGE,{"derivedFrom":sQuery(id+"F15.wireOp",EDGE,"E64.MirrorCS")}),-1.0]])]});
            extrude(context, id + "F16", {"entities" : qUnion([Q0, Q1]), "depth" : 6.38 * mm, "offsetDistance" : 25.4 * mm});
        }
        {
            var Q0;
            Q0=qCreatedBy(makeId("Top.planeOp"),FACE);
            var sketch = newSketch(context, id + "F17", { "sketchPlane" : qUnion([Q0])});
            skPoint(sketch, "E90.0", {"position": v(-241.3, 107.95) * mm});
            skPoint(sketch, "E90.1", {"position": v(120.65, 107.95) * mm});
            skLineSegment(sketch, "E91.bottom", {"start": v(101.6, 201.7) * mm, "end": v(-222.25, 201.7) * mm});
            skLineSegment(sketch, "E91.top", {"start": v(101.6, 239.8) * mm, "end": v(-222.25, 239.8) * mm});
            skLineSegment(sketch, "E91.left", {"start": v(101.6, 201.7) * mm, "end": v(101.6, 239.8) * mm});
            skLineSegment(sketch, "E91.right", {"start": v(-222.25, 201.7) * mm, "end": v(-222.25, 239.8) * mm});
            skPoint(sketch, "E91.middle", {"position": v(-60.33, 220.75) * mm});
            skLineSegment(sketch, "E92.bottom", {"start": v(104.77, 226.92) * mm, "end": v(-225.43, 226.92) * mm});
            skLineSegment(sketch, "E92.top", {"start": v(104.77, 233.45) * mm, "end": v(-225.43, 233.45) * mm});
            skLineSegment(sketch, "E92.left", {"start": v(104.78, 226.92) * mm, "end": v(104.78, 233.45) * mm});
            skLineSegment(sketch, "E92.right", {"start": v(-225.43, 226.92) * mm, "end": v(-225.43, 233.45) * mm});
            skPoint(sketch, "E92.middle", {"position": v(-60.33, 230.18) * mm});
            skSolve(sketch);
        }
        {
            var Q0;
            {var subQ0=sQuery(id+"F17.wireOp",EDGE,"E91.bottom");Q0=makeQuery(id+"F17.imprint","IMPRINT",FACE,{"disambiguationData":[TD([[makeQuery(id+"F17.imprint","IMPRINT",EDGE,{"derivedFrom":subQ0}),-1.0]])]});}
            var Q1;
            {var subQ0=sQuery(id+"F17.wireOp",EDGE,"E92.bottom");var subQ1=sQuery(id+"F17.wireOp",EDGE,"E91.left");var subQ2=makeQuery(id+"F17.imprint","INTERSECT",VERTEX,{"derivedFrom":[subQ1,subQ0]});Q1=makeQuery(id+"F17.imprint","IMPRINT",FACE,{"disambiguationData":[TD([[makeQuery(id+"F17.imprint","IMPRINT",EDGE,{"disambiguationData":[TD([[subQ2,-1.0]])],"derivedFrom":subQ1}),1.0]])]});}
            var Q2;
            {var subQ0=sQuery(id+"F17.wireOp",EDGE,"E91.top");Q2=makeQuery(id+"F17.imprint","IMPRINT",FACE,{"disambiguationData":[TD([[makeQuery(id+"F17.imprint","IMPRINT",EDGE,{"derivedFrom":subQ0}),1.0]])]});}
            extrude(context, id + "F18", {"entities" : qUnion([Q0, Q1, Q2]), "oppositeDirection" : true, "depth" : 12.7 * mm, "offsetDistance" : 25.4 * mm});
        }
        {
            var Q0;
            {var subQ0=sQuery(id+"F17.wireOp",EDGE,"E91.top");Q0=makeQuery(id+"F17.imprint","IMPRINT",FACE,{"disambiguationData":[TD([[makeQuery(id+"F17.imprint","IMPRINT",EDGE,{"derivedFrom":subQ0}),1.0]])]});}
            var Q1;
            {var subQ0=sQuery(id+"F17.wireOp",EDGE,"E91.bottom");Q1=makeQuery(id+"F17.imprint","IMPRINT",FACE,{"disambiguationData":[TD([[makeQuery(id+"F17.imprint","IMPRINT",EDGE,{"derivedFrom":subQ0}),-1.0]])]});}
            extrude(context, id + "F19", {"entities" : qUnion([Q0, Q1]), "operationType" : NewBodyOperationType.ADD, "depth" : 6.35 * mm, "offsetDistance" : 25.4 * mm});
        }
        {
            var Q0;
            Q0=qCreatedBy(makeId("Top.planeOp"),FACE);
            var sketch = newSketch(context, id + "F20", { "sketchPlane" : qUnion([Q0])});
            skLineSegment(sketch, "E93.bottom", {"start": v(-212.1, 410.8) * mm, "end": v(82.4, 410.8) * mm});
            skLineSegment(sketch, "E93.top", {"start": v(-212.1, 590) * mm, "end": v(82.4, 590) * mm});
            skLineSegment(sketch, "E93.left", {"start": v(-224.8, 423.5) * mm, "end": v(-224.8, 577.3) * mm});
            skLineSegment(sketch, "E93.right", {"start": v(95.1, 423.5) * mm, "end": v(95.1, 577.3) * mm});
            skCircle(sketch, "E94", {"center": v(-191.77, 567.15) * mm, "radius": 9 * mm});
            skCircle(sketch, "E95", {"center": v(-191.77, 433.67) * mm, "radius": 9 * mm});
            skCircle(sketch, "E96", {"center": v(62.08, 567.15) * mm, "radius": 9 * mm});
            skCircle(sketch, "E97", {"center": v(62.08, 433.67) * mm, "radius": 9 * mm});
            skPoint(sketch, "E98.visualSharp", {"position": v(-224.8, 590) * mm});
            skArc(sketch, "E98.filletArc", {"start": v(-212.1, 590) * mm, "mid": v(-221.07, 586.29) * mm, "end": v(-224.8, 577.3) * mm});
            skPoint(sketch, "E99.visualSharp", {"position": v(95.1, 590) * mm});
            skArc(sketch, "E99.filletArc", {"start": v(95.1, 577.3) * mm, "mid": v(91.38, 586.29) * mm, "end": v(82.4, 590) * mm});
            skPoint(sketch, "E100.visualSharp", {"position": v(-224.8, 410.8) * mm});
            skArc(sketch, "E100.filletArc", {"start": v(-224.8, 423.5) * mm, "mid": v(-221.07, 414.53) * mm, "end": v(-212.1, 410.8) * mm});
            skPoint(sketch, "E101.visualSharp", {"position": v(95.1, 410.8) * mm});
            skArc(sketch, "E101.filletArc", {"start": v(82.4, 410.8) * mm, "mid": v(91.38, 414.53) * mm, "end": v(95.1, 423.5) * mm});
            skPoint(sketch, "E102", {"position": v(-224.8, 500.4) * mm});
            skPoint(sketch, "E103", {"position": v(95.1, 500.4) * mm});
            skPoint(sketch, "E104", {"position": v(-64.85, 590) * mm});
            skPoint(sketch, "E105", {"position": v(-64.85, 410.8) * mm});
            skSolve(sketch);
        }
        {
            var Q0;
            Q0=makeQuery(id+"F20.imprint","IMPRINT",FACE,{"disambiguationData":[TD([[makeQuery(id+"F20.imprint","IMPRINT",EDGE,{"derivedFrom":sQuery(id+"F20.wireOp",EDGE,"E93.bottom")}),1.0]])]});
            extrude(context, id + "F21", {"entities" : qUnion([Q0]), "depth" : 3 * mm, "offsetDistance" : 25.4 * mm});
        }
        {
            var Q0;
            Q0=makeQuery(id+"F0.imprint","IMPRINT",FACE,{"disambiguationData":[TD([[makeQuery(id+"F0.imprint","IMPRINT",EDGE,{"derivedFrom":sQuery(id+"F0.wireOp",EDGE,"E3")}),-1.0]])]});
            extrude(context, id + "F22", {"entities" : qUnion([Q0]), "operationType" : NewBodyOperationType.REMOVE, "endBound" : BoundingType.SYMMETRIC, "depth" : 12.7 * mm, "offsetDistance" : 25.4 * mm});
        }
        {
            var Q0;
            Q0=qCreatedBy(makeId("Top.planeOp"),FACE);
            var sketch = newSketch(context, id + "F23", { "sketchPlane" : qUnion([Q0])});
            skLineSegment(sketch, "E106.MirrorCS", {"start": v(8.55, -872.45) * mm, "end": v(-3.45, -872.45) * mm});
            skLineSegment(sketch, "E107.MirrorCS", {"start": v(-11.95, -872.45) * mm, "end": v(-23.95, -872.45) * mm});
            skLineSegment(sketch, "E108.MirrorCS", {"start": v(8.55, -974.05) * mm, "end": v(-3.45, -974.05) * mm});
            skLineSegment(sketch, "E109.MirrorCS", {"start": v(-32.45, -974.05) * mm, "end": v(-44.45, -974.05) * mm});
            skLineSegment(sketch, "E110.MirrorCS", {"start": v(-11.95, -974.05) * mm, "end": v(-23.95, -974.05) * mm});
            skLineSegment(sketch, "E111.MirrorCS", {"start": v(-32.45, -872.45) * mm, "end": v(-44.45, -872.45) * mm});
            skLineSegment(sketch, "E112.MirrorCS", {"start": v(-11.95, -974.05) * mm, "end": v(-11.95, -872.45) * mm});
            skLineSegment(sketch, "E113.MirrorCS", {"start": v(8.55, -974.05) * mm, "end": v(8.55, -872.45) * mm});
            skLineSegment(sketch, "E114.MirrorCS", {"start": v(-32.45, -974.05) * mm, "end": v(-32.45, -872.45) * mm});
            skLineSegment(sketch, "E115.MirrorCS", {"start": v(-3.45, -974.05) * mm, "end": v(-3.45, -872.45) * mm});
            skLineSegment(sketch, "E116.MirrorCS", {"start": v(107.95, -1048.9) * mm, "end": v(107.95, -855.25) * mm});
            skLineSegment(sketch, "E117.MirrorCS", {"start": v(-228.6, -1048.9) * mm, "end": v(-228.6, -855.25) * mm});
            skLineSegment(sketch, "E118.MirrorCS", {"start": v(107.95, -1048.9) * mm, "end": v(-228.6, -1048.9) * mm});
            skLineSegment(sketch, "E119.MirrorCS", {"start": v(107.95, -855.25) * mm, "end": v(-228.6, -855.25) * mm});
            skLineSegment(sketch, "E120.MirrorCS", {"start": v(-23.95, -974.05) * mm, "end": v(-23.95, -872.45) * mm});
            skLineSegment(sketch, "E121.MirrorCS", {"start": v(-44.45, -974.05) * mm, "end": v(-44.45, -872.45) * mm});
            skLineSegment(sketch, "E122.bottom", {"start": v(-209.2, -866.45) * mm, "end": v(-50.45, -866.45) * mm});
            skLineSegment(sketch, "E122.top", {"start": v(-209.2, -910.9) * mm, "end": v(-50.45, -910.9) * mm});
            skLineSegment(sketch, "E122.left", {"start": v(-209.2, -866.45) * mm, "end": v(-209.2, -910.9) * mm});
            skLineSegment(sketch, "E122.right", {"start": v(-50.45, -866.45) * mm, "end": v(-50.45, -910.9) * mm});
            skPoint(sketch, "E123.middle.positionSnap0", {"position": v(107.95, -952.07) * mm});
            skPoint(sketch, "E123.centerSnap0", {"position": v(107.95, -952.07) * mm});
            skCircle(sketch, "E124", {"center": v(-129.82, -982.86) * mm, "radius": 44.5 * mm});
            skCircle(sketch, "E125", {"center": v(-171.07, -941.6) * mm, "radius": 2.5 * mm});
            skCircle(sketch, "E126", {"center": v(-88.57, -941.6) * mm, "radius": 2.5 * mm});
            skCircle(sketch, "E127", {"center": v(-171.07, -1024.1) * mm, "radius": 2.5 * mm});
            skCircle(sketch, "E128", {"center": v(-88.57, -1024.11) * mm, "radius": 2.5 * mm});
            skCircle(sketch, "E129", {"center": v(-177.93, -927.4) * mm, "radius": 2 * mm});
            skCircle(sketch, "E130", {"center": v(-81.73, -927.4) * mm, "radius": 2 * mm});
            skLineSegment(sketch, "E131.bottom", {"start": v(95.25, -898.5) * mm, "end": v(31.75, -898.5) * mm});
            skLineSegment(sketch, "E131.top", {"start": v(95.25, -1023.5) * mm, "end": v(31.75, -1023.5) * mm});
            skLineSegment(sketch, "E131.left", {"start": v(95.25, -898.5) * mm, "end": v(95.25, -1023.5) * mm});
            skLineSegment(sketch, "E131.right", {"start": v(31.75, -898.5) * mm, "end": v(31.75, -1023.5) * mm});
            skLineSegment(sketch, "E132", {"start": v(-210.12, -860.45) * mm, "end": v(11.47, -860.45) * mm});
            skLineSegment(sketch, "E133", {"start": v(11.47, -979.45) * mm, "end": v(-47.37, -979.45) * mm});
            skLineSegment(sketch, "E134", {"start": v(-52.45, -974.37) * mm, "end": v(-52.45, -921.98) * mm});
            skLineSegment(sketch, "E135", {"start": v(-215.2, -911.82) * mm, "end": v(-215.2, -865.53) * mm});
            skPoint(sketch, "E136.visualSharp", {"position": v(-215.2, -860.45) * mm});
            skArc(sketch, "E136.filletArc", {"start": v(-210.12, -860.45) * mm, "mid": v(-213.71, -861.94) * mm, "end": v(-215.2, -865.53) * mm});
            skPoint(sketch, "E137.visualSharp", {"position": v(-215.2, -916.9) * mm});
            skArc(sketch, "E137.filletArc", {"start": v(-215.2, -911.82) * mm, "mid": v(-213.71, -915.41) * mm, "end": v(-210.12, -916.9) * mm});
            skPoint(sketch, "E138.visualSharp", {"position": v(16.55, -860.45) * mm});
            skArc(sketch, "E138.filletArc", {"start": v(16.55, -865.53) * mm, "mid": v(15.06, -861.94) * mm, "end": v(11.47, -860.45) * mm});
            skPoint(sketch, "E139.visualSharp", {"position": v(-52.45, -916.9) * mm});
            skArc(sketch, "E139.filletArc", {"start": v(-52.45, -921.98) * mm, "mid": v(-53.94, -918.39) * mm, "end": v(-57.53, -916.9) * mm});
            skLineSegment(sketch, "E140.bottom", {"start": v(-47, -974.05) * mm, "end": v(11.09, -974.05) * mm});
            skLineSegment(sketch, "E140.top", {"start": v(-47, -979.45) * mm, "end": v(11.09, -979.45) * mm});
            skLineSegment(sketch, "E140.left", {"start": v(-47, -974.05) * mm, "end": v(-47, -979.45) * mm});
            skLineSegment(sketch, "E140.right", {"start": v(11.09, -974.05) * mm, "end": v(11.09, -979.45) * mm});
            skPoint(sketch, "E141.visualSharp", {"position": v(-52.45, -979.45) * mm});
            skArc(sketch, "E141.filletArc", {"start": v(-52.45, -974.37) * mm, "mid": v(-50.96, -977.96) * mm, "end": v(-47.37, -979.45) * mm});
            skPoint(sketch, "E142.visualSharp", {"position": v(16.55, -979.45) * mm});
            skArc(sketch, "E142.filletArc", {"start": v(11.47, -979.45) * mm, "mid": v(15.06, -977.96) * mm, "end": v(16.55, -974.37) * mm});
            skCircle(sketch, "E143", {"center": v(24.52, -880.77) * mm, "radius": 2 * mm});
            skLineSegment(sketch, "E144.top", {"start": v(-180.47, -932.14) * mm, "end": v(-175.39, -932.14) * mm});
            skLineSegment(sketch, "E144.left", {"start": v(-185.55, -921.98) * mm, "end": v(-185.55, -927.06) * mm});
            skLineSegment(sketch, "E144.right", {"start": v(-170.3, -921.98) * mm, "end": v(-170.3, -927.06) * mm});
            skLineSegment(sketch, "E145.top", {"start": v(-84.27, -932.14) * mm, "end": v(-79.19, -932.14) * mm});
            skLineSegment(sketch, "E145.left", {"start": v(-89.35, -921.98) * mm, "end": v(-89.35, -927.06) * mm});
            skLineSegment(sketch, "E145.right", {"start": v(-74.1, -921.98) * mm, "end": v(-74.1, -927.06) * mm});
            skPoint(sketch, "E146.visualSharp", {"position": v(-185.55, -932.14) * mm});
            skArc(sketch, "E146.filletArc", {"start": v(-185.55, -927.06) * mm, "mid": v(-184.06, -930.65) * mm, "end": v(-180.47, -932.14) * mm});
            skPoint(sketch, "E147.visualSharp", {"position": v(-170.3, -932.14) * mm});
            skArc(sketch, "E147.filletArc", {"start": v(-175.39, -932.14) * mm, "mid": v(-171.8, -930.65) * mm, "end": v(-170.3, -927.06) * mm});
            skPoint(sketch, "E148.visualSharp", {"position": v(-89.35, -932.14) * mm});
            skArc(sketch, "E148.filletArc", {"start": v(-89.35, -927.06) * mm, "mid": v(-87.86, -930.65) * mm, "end": v(-84.27, -932.14) * mm});
            skPoint(sketch, "E149.visualSharp", {"position": v(-74.1, -932.14) * mm});
            skArc(sketch, "E149.filletArc", {"start": v(-79.19, -932.14) * mm, "mid": v(-75.6, -930.65) * mm, "end": v(-74.1, -927.06) * mm});
            skLineSegment(sketch, "E150", {"start": v(-190.63, -916.9) * mm, "end": v(-210.12, -916.9) * mm});
            skLineSegment(sketch, "E151", {"start": v(-165.23, -916.9) * mm, "end": v(-94.43, -916.9) * mm});
            skLineSegment(sketch, "E152", {"start": v(-69.03, -916.9) * mm, "end": v(-57.53, -916.9) * mm});
            skArc(sketch, "E153.filletArc", {"start": v(-185.55, -921.98) * mm, "mid": v(-187.03, -918.39) * mm, "end": v(-190.63, -916.9) * mm});
            skArc(sketch, "E154.filletArc", {"start": v(-165.23, -916.9) * mm, "mid": v(-168.82, -918.39) * mm, "end": v(-170.3, -921.98) * mm});
            skArc(sketch, "E155.filletArc", {"start": v(-89.35, -921.98) * mm, "mid": v(-90.83, -918.39) * mm, "end": v(-94.43, -916.9) * mm});
            skArc(sketch, "E156.filletArc", {"start": v(-69.03, -916.9) * mm, "mid": v(-72.62, -918.39) * mm, "end": v(-74.1, -921.98) * mm});
            skLineSegment(sketch, "E157.bottom", {"start": v(21.63, -873.15) * mm, "end": v(24.17, -873.15) * mm});
            skLineSegment(sketch, "E157.top", {"start": v(21.63, -888.39) * mm, "end": v(24.17, -888.39) * mm});
            skLineSegment(sketch, "E157.right", {"start": v(29.25, -878.23) * mm, "end": v(29.25, -883.3) * mm});
            skPoint(sketch, "E158.visualSharp", {"position": v(29.25, -873.15) * mm});
            skArc(sketch, "E158.filletArc", {"start": v(29.25, -878.23) * mm, "mid": v(27.76, -874.64) * mm, "end": v(24.17, -873.15) * mm});
            skPoint(sketch, "E159.visualSharp", {"position": v(29.25, -888.39) * mm});
            skArc(sketch, "E159.filletArc", {"start": v(24.17, -888.39) * mm, "mid": v(27.76, -886.9) * mm, "end": v(29.25, -883.3) * mm});
            skLineSegment(sketch, "E160", {"start": v(16.55, -865.53) * mm, "end": v(16.55, -868.07) * mm});
            skLineSegment(sketch, "E161", {"start": v(16.55, -893.47) * mm, "end": v(16.55, -974.37) * mm});
            skPoint(sketch, "E162.visualSharp", {"position": v(16.55, -873.15) * mm});
            skArc(sketch, "E162.filletArc", {"start": v(16.55, -868.07) * mm, "mid": v(18.04, -871.66) * mm, "end": v(21.63, -873.15) * mm});
            skPoint(sketch, "E163.visualSharp", {"position": v(16.55, -888.39) * mm});
            skArc(sketch, "E163.filletArc", {"start": v(21.63, -888.39) * mm, "mid": v(18.04, -889.88) * mm, "end": v(16.55, -893.47) * mm});
            skSolve(sketch);
        }
        {
            var Q0;
            Q0=makeQuery(id+"F23.imprint","IMPRINT",FACE,{"disambiguationData":[TD([[makeQuery(id+"F23.imprint","IMPRINT",EDGE,{"derivedFrom":sQuery(id+"F23.wireOp",EDGE,"E106.MirrorCS")}),-1.0]])]});
            var Q1;
            Q1=makeQuery(id+"F23.imprint","IMPRINT",FACE,{"disambiguationData":[TD([[makeQuery(id+"F23.imprint","IMPRINT",EDGE,{"derivedFrom":sQuery(id+"F23.wireOp",EDGE,"CCQa77y0-4UvF-OhPD-uDzf-5uZMRSXnv3wF")}),-1.0]])]});
            var Q2;
            Q2=makeQuery(id+"F23.imprint","IMPRINT",FACE,{"disambiguationData":[TD([[makeQuery(id+"F23.imprint","IMPRINT",EDGE,{"derivedFrom":sQuery(id+"F23.wireOp",EDGE,"E106.MirrorCS")}),-1.0]])]});
            var Q3;
            {var subQ0=sQuery(id+"F23.wireOp",EDGE,"E133");var subQ1=sQuery(id+"F23.wireOp",EDGE,"zq396qQx-WNYs-cslI-mTqz-GNkz0O8GxnUQ");var subQ2=makeQuery(id+"F23.imprint","INTERSECT",VERTEX,{"derivedFrom":[subQ1,subQ0]});Q3=makeQuery(id+"F23.imprint","IMPRINT",FACE,{"disambiguationData":[TD([[makeQuery(id+"F23.imprint","IMPRINT",EDGE,{"disambiguationData":[TD([[subQ2,1.0]])],"derivedFrom":subQ1}),-1.0]])]});}
            var Q4;
            Q4=makeQuery(id+"F23.imprint","IMPRINT",FACE,{"disambiguationData":[TD([[makeQuery(id+"F23.imprint","IMPRINT",EDGE,{"derivedFrom":sQuery(id+"F23.wireOp",EDGE,"heEkxspo-XaDG-pVp8-72LV-1jOJynqTQx8I")}),-1.0]])]});
            var Q5;
            {var subQ6=sQuery(id+"F23.wireOp",EDGE,"E108.MirrorCS");Q5=makeQuery(id+"F23.imprint","IMPRINT",FACE,{"disambiguationData":[TD([[makeQuery(id+"F23.imprint","IMPRINT",EDGE,{"derivedFrom":subQ6}),1.0]])]});}
            extrude(context, id + "F24", {"entities" : qUnion([Q0, Q1, Q2, Q3, Q4, Q5]), "depth" : 2 * mm, "offsetDistance" : 25.4 * mm});
        }
        {
            var Q0;
            {var subQ6=sQuery(id+"F23.wireOp",EDGE,"E108.MirrorCS");Q0=makeQuery(id+"F23.imprint","IMPRINT",FACE,{"disambiguationData":[TD([[makeQuery(id+"F23.imprint","IMPRINT",EDGE,{"derivedFrom":subQ6}),1.0]])]});}
            extrude(context, id + "F25", {"entities" : qUnion([Q0]), "operationType" : NewBodyOperationType.ADD, "oppositeDirection" : true, "depth" : 10 * mm, "offsetDistance" : 25.4 * mm});
        }
        {
            var Q0;
            Q0=qCreatedBy(makeId("Top.planeOp"),FACE);
            var sketch = newSketch(context, id + "F26", { "sketchPlane" : qUnion([Q0])});
            skLineSegment(sketch, "E164.MirrorCS", {"start": v(8.55, -1035.14) * mm, "end": v(-3.45, -1035.14) * mm});
            skLineSegment(sketch, "E165.MirrorCS", {"start": v(-11.95, -1035.15) * mm, "end": v(-23.95, -1035.15) * mm});
            skLineSegment(sketch, "E166.MirrorCS", {"start": v(8.55, -1136.75) * mm, "end": v(-3.45, -1136.75) * mm});
            skLineSegment(sketch, "E167.MirrorCS", {"start": v(-32.45, -1136.75) * mm, "end": v(-44.45, -1136.75) * mm});
            skLineSegment(sketch, "E168.MirrorCS", {"start": v(-11.95, -1136.75) * mm, "end": v(-23.95, -1136.75) * mm});
            skLineSegment(sketch, "E169.MirrorCS", {"start": v(-32.45, -1035.15) * mm, "end": v(-44.45, -1035.15) * mm});
            skLineSegment(sketch, "E170.MirrorCS", {"start": v(-11.95, -1136.75) * mm, "end": v(-11.95, -1035.15) * mm});
            skLineSegment(sketch, "E171.MirrorCS", {"start": v(8.55, -1136.75) * mm, "end": v(8.55, -1035.14) * mm});
            skLineSegment(sketch, "E172.MirrorCS", {"start": v(-32.45, -1136.75) * mm, "end": v(-32.45, -1035.15) * mm});
            skLineSegment(sketch, "E173.MirrorCS", {"start": v(-3.45, -1136.75) * mm, "end": v(-3.45, -1035.14) * mm});
            skLineSegment(sketch, "E174.MirrorCS", {"start": v(107.95, -1211.6) * mm, "end": v(107.95, -1017.95) * mm});
            skLineSegment(sketch, "E175.MirrorCS", {"start": v(-228.6, -1211.6) * mm, "end": v(-228.6, -1017.95) * mm});
            skLineSegment(sketch, "E176.MirrorCS", {"start": v(107.95, -1211.6) * mm, "end": v(-228.6, -1211.6) * mm});
            skLineSegment(sketch, "E177.MirrorCS", {"start": v(107.95, -1017.95) * mm, "end": v(-228.6, -1017.95) * mm});
            skLineSegment(sketch, "E178.MirrorCS", {"start": v(-23.95, -1136.75) * mm, "end": v(-23.95, -1035.15) * mm});
            skLineSegment(sketch, "E179.MirrorCS", {"start": v(-44.45, -1136.75) * mm, "end": v(-44.45, -1035.15) * mm});
            skLineSegment(sketch, "E180.bottom", {"start": v(-209.2, -1029.15) * mm, "end": v(-50.45, -1029.15) * mm});
            skLineSegment(sketch, "E180.top", {"start": v(-209.2, -1073.6) * mm, "end": v(-50.45, -1073.6) * mm});
            skLineSegment(sketch, "E180.left", {"start": v(-209.2, -1029.15) * mm, "end": v(-209.2, -1073.6) * mm});
            skLineSegment(sketch, "E180.right", {"start": v(-50.45, -1029.15) * mm, "end": v(-50.45, -1073.6) * mm});
            skPoint(sketch, "E181.middle.positionSnap0", {"position": v(107.95, -1114.77) * mm});
            skPoint(sketch, "E181.centerSnap0", {"position": v(107.95, -1114.77) * mm});
            skCircle(sketch, "E182", {"center": v(-129.82, -1145.56) * mm, "radius": 44.5 * mm});
            skCircle(sketch, "E183", {"center": v(-171.07, -1104.3) * mm, "radius": 2.5 * mm});
            skCircle(sketch, "E184", {"center": v(-88.57, -1104.3) * mm, "radius": 2.5 * mm});
            skCircle(sketch, "E185", {"center": v(-171.07, -1186.8) * mm, "radius": 2.5 * mm});
            skCircle(sketch, "E186", {"center": v(-88.57, -1186.8) * mm, "radius": 2.5 * mm});
            skCircle(sketch, "E187", {"center": v(-177.93, -1090.1) * mm, "radius": 2 * mm});
            skCircle(sketch, "E188", {"center": v(-81.73, -1090.1) * mm, "radius": 2 * mm});
            skLineSegment(sketch, "E189.bottom", {"start": v(95.25, -1061.2) * mm, "end": v(31.75, -1061.2) * mm});
            skLineSegment(sketch, "E189.top", {"start": v(95.25, -1186.2) * mm, "end": v(31.75, -1186.2) * mm});
            skLineSegment(sketch, "E189.left", {"start": v(95.25, -1061.2) * mm, "end": v(95.25, -1186.2) * mm});
            skLineSegment(sketch, "E189.right", {"start": v(31.75, -1061.2) * mm, "end": v(31.75, -1186.2) * mm});
            skLineSegment(sketch, "E190", {"start": v(-210.12, -1023.15) * mm, "end": v(11.47, -1023.15) * mm});
            skLineSegment(sketch, "E191", {"start": v(11.47, -1142.14) * mm, "end": v(-47.37, -1142.14) * mm});
            skLineSegment(sketch, "E192", {"start": v(-52.45, -1137.06) * mm, "end": v(-52.45, -1084.68) * mm});
            skLineSegment(sketch, "E193", {"start": v(-215.2, -1074.5) * mm, "end": v(-215.2, -1028.23) * mm});
            skPoint(sketch, "E194.visualSharp", {"position": v(-215.2, -1023.15) * mm});
            skArc(sketch, "E194.filletArc", {"start": v(-210.12, -1023.15) * mm, "mid": v(-213.71, -1024.63) * mm, "end": v(-215.2, -1028.23) * mm});
            skPoint(sketch, "E195.visualSharp", {"position": v(-215.2, -1079.58) * mm});
            skArc(sketch, "E195.filletArc", {"start": v(-215.2, -1074.5) * mm, "mid": v(-213.71, -1078.09) * mm, "end": v(-210.12, -1079.58) * mm});
            skPoint(sketch, "E196.visualSharp", {"position": v(16.55, -1023.15) * mm});
            skArc(sketch, "E196.filletArc", {"start": v(16.55, -1028.23) * mm, "mid": v(15.06, -1024.63) * mm, "end": v(11.47, -1023.15) * mm});
            skPoint(sketch, "E197.visualSharp", {"position": v(-52.45, -1079.58) * mm});
            skArc(sketch, "E197.filletArc", {"start": v(-52.45, -1084.68) * mm, "mid": v(-53.94, -1081.08) * mm, "end": v(-57.53, -1079.6) * mm});
            skLineSegment(sketch, "E198.bottom", {"start": v(-47, -1136.75) * mm, "end": v(11.09, -1136.75) * mm});
            skLineSegment(sketch, "E198.top", {"start": v(-47, -1142.14) * mm, "end": v(11.09, -1142.14) * mm});
            skLineSegment(sketch, "E198.left", {"start": v(-47, -1136.75) * mm, "end": v(-47, -1142.14) * mm});
            skLineSegment(sketch, "E198.right", {"start": v(11.09, -1136.75) * mm, "end": v(11.09, -1142.14) * mm});
            skPoint(sketch, "E199.visualSharp", {"position": v(-52.45, -1142.14) * mm});
            skArc(sketch, "E199.filletArc", {"start": v(-52.45, -1137.06) * mm, "mid": v(-50.96, -1140.66) * mm, "end": v(-47.37, -1142.14) * mm});
            skPoint(sketch, "E200.visualSharp", {"position": v(13.03, -1142.14) * mm});
            skArc(sketch, "E200.filletArc", {"start": v(11.47, -1142.14) * mm, "mid": v(15.06, -1140.66) * mm, "end": v(16.55, -1137.06) * mm});
            skCircle(sketch, "E201", {"center": v(24.52, -1043.47) * mm, "radius": 2 * mm});
            skLineSegment(sketch, "E202.top", {"start": v(-180.47, -1094.84) * mm, "end": v(-175.39, -1094.84) * mm});
            skLineSegment(sketch, "E202.left", {"start": v(-185.55, -1084.66) * mm, "end": v(-185.55, -1089.76) * mm});
            skLineSegment(sketch, "E202.right", {"start": v(-170.3, -1084.68) * mm, "end": v(-170.3, -1089.76) * mm});
            skLineSegment(sketch, "E203.top", {"start": v(-84.27, -1094.84) * mm, "end": v(-79.19, -1094.84) * mm});
            skLineSegment(sketch, "E203.left", {"start": v(-89.35, -1084.68) * mm, "end": v(-89.35, -1089.76) * mm});
            skLineSegment(sketch, "E203.right", {"start": v(-74.1, -1084.68) * mm, "end": v(-74.1, -1089.76) * mm});
            skPoint(sketch, "E204.visualSharp", {"position": v(-185.55, -1094.84) * mm});
            skArc(sketch, "E204.filletArc", {"start": v(-185.55, -1089.76) * mm, "mid": v(-184.06, -1093.35) * mm, "end": v(-180.47, -1094.84) * mm});
            skPoint(sketch, "E205.visualSharp", {"position": v(-170.3, -1094.84) * mm});
            skArc(sketch, "E205.filletArc", {"start": v(-175.39, -1094.84) * mm, "mid": v(-171.8, -1093.35) * mm, "end": v(-170.3, -1089.76) * mm});
            skPoint(sketch, "E206.visualSharp", {"position": v(-89.35, -1094.84) * mm});
            skArc(sketch, "E206.filletArc", {"start": v(-89.35, -1089.76) * mm, "mid": v(-87.86, -1093.35) * mm, "end": v(-84.27, -1094.84) * mm});
            skPoint(sketch, "E207.visualSharp", {"position": v(-74.1, -1094.84) * mm});
            skArc(sketch, "E207.filletArc", {"start": v(-79.19, -1094.84) * mm, "mid": v(-75.6, -1093.35) * mm, "end": v(-74.1, -1089.76) * mm});
            skLineSegment(sketch, "E208", {"start": v(-190.63, -1079.58) * mm, "end": v(-210.12, -1079.58) * mm});
            skLineSegment(sketch, "E209", {"start": v(-165.23, -1079.6) * mm, "end": v(-94.43, -1079.6) * mm});
            skLineSegment(sketch, "E210", {"start": v(-69.03, -1079.6) * mm, "end": v(-57.53, -1079.6) * mm});
            skArc(sketch, "E211.filletArc", {"start": v(-185.55, -1084.66) * mm, "mid": v(-187.03, -1081.06) * mm, "end": v(-190.63, -1079.58) * mm});
            skArc(sketch, "E212.filletArc", {"start": v(-165.23, -1079.6) * mm, "mid": v(-168.82, -1081.08) * mm, "end": v(-170.3, -1084.68) * mm});
            skArc(sketch, "E213.filletArc", {"start": v(-89.35, -1084.68) * mm, "mid": v(-90.83, -1081.08) * mm, "end": v(-94.43, -1079.6) * mm});
            skArc(sketch, "E214.filletArc", {"start": v(-69.03, -1079.6) * mm, "mid": v(-72.62, -1081.08) * mm, "end": v(-74.1, -1084.68) * mm});
            skLineSegment(sketch, "E215.bottom", {"start": v(21.63, -1035.85) * mm, "end": v(24.17, -1035.85) * mm});
            skLineSegment(sketch, "E215.top", {"start": v(21.63, -1051.09) * mm, "end": v(24.17, -1051.09) * mm});
            skLineSegment(sketch, "E215.right", {"start": v(29.25, -1040.93) * mm, "end": v(29.25, -1046) * mm});
            skPoint(sketch, "E216.visualSharp", {"position": v(29.25, -1035.85) * mm});
            skArc(sketch, "E216.filletArc", {"start": v(29.25, -1040.93) * mm, "mid": v(27.76, -1037.33) * mm, "end": v(24.17, -1035.85) * mm});
            skPoint(sketch, "E217.visualSharp", {"position": v(29.25, -1051.09) * mm});
            skArc(sketch, "E217.filletArc", {"start": v(24.17, -1051.09) * mm, "mid": v(27.76, -1049.6) * mm, "end": v(29.25, -1046) * mm});
            skLineSegment(sketch, "E218", {"start": v(16.55, -1028.23) * mm, "end": v(16.55, -1030.77) * mm});
            skLineSegment(sketch, "E219", {"start": v(16.55, -1056.17) * mm, "end": v(16.55, -1137.06) * mm});
            skPoint(sketch, "E220.visualSharp", {"position": v(16.55, -1035.85) * mm});
            skArc(sketch, "E220.filletArc", {"start": v(16.55, -1030.77) * mm, "mid": v(18.04, -1034.36) * mm, "end": v(21.63, -1035.85) * mm});
            skPoint(sketch, "E221.visualSharp", {"position": v(16.55, -1051.09) * mm});
            skArc(sketch, "E221.filletArc", {"start": v(21.63, -1051.09) * mm, "mid": v(18.04, -1052.57) * mm, "end": v(16.55, -1056.17) * mm});
            skLineSegment(sketch, "E222.bottom", {"start": v(-212.2, -1076.6) * mm, "end": v(-47.45, -1076.6) * mm});
            skLineSegment(sketch, "E222.top", {"start": v(-212.2, -1026.15) * mm, "end": v(-47.45, -1026.15) * mm});
            skLineSegment(sketch, "E222.left", {"start": v(-212.2, -1076.6) * mm, "end": v(-212.2, -1026.15) * mm});
            skLineSegment(sketch, "E222.right", {"start": v(-47.45, -1076.6) * mm, "end": v(-47.45, -1026.15) * mm});
            skLineSegment(sketch, "E223.bottom", {"start": v(-47.45, -1136.75) * mm, "end": v(11.55, -1136.75) * mm});
            skLineSegment(sketch, "E223.top", {"start": v(-47.45, -1032.15) * mm, "end": v(11.55, -1032.15) * mm});
            skLineSegment(sketch, "E223.left", {"start": v(-47.45, -1136.75) * mm, "end": v(-47.45, -1032.15) * mm});
            skLineSegment(sketch, "E223.right", {"start": v(11.55, -1136.75) * mm, "end": v(11.55, -1032.15) * mm});
            skSolve(sketch);
        }
        {
            var Q0;
            Q0=makeQuery(id+"F26.imprint","IMPRINT",FACE,{"disambiguationData":[TD([[makeQuery(id+"F26.imprint","IMPRINT",EDGE,{"derivedFrom":sQuery(id+"F26.wireOp",EDGE,"E174.MirrorCS")}),1.0]])]});
            var Q1;
            Q1=makeQuery(id+"F26.imprint","IMPRINT",FACE,{"disambiguationData":[TD([[makeQuery(id+"F26.imprint","IMPRINT",EDGE,{"derivedFrom":sQuery(id+"F26.wireOp",EDGE,"E187")}),-1.0]])]});
            extrude(context, id + "F27", {"entities" : qUnion([Q0, Q1]), "depth" : 6.4 * mm, "offsetDistance" : 25.4 * mm});
        }
        {
            var Q0;
            Q0=makeQuery(id+"F26.imprint","IMPRINT",FACE,{"disambiguationData":[TD([[makeQuery(id+"F26.imprint","IMPRINT",EDGE,{"derivedFrom":sQuery(id+"F26.wireOp",EDGE,"E187")}),-1.0]])]});
            extrude(context, id + "F28", {"entities" : qUnion([Q0]), "operationType" : NewBodyOperationType.REMOVE, "depth" : 6.4 * mm, "offsetDistance" : 25.4 * mm, "hasSecondDirection" : true, "secondDirectionOppositeDirection" : false, "secondDirectionDepth" : 4 * mm});
        }
        {
            var Q0;
            Q0=qCreatedBy(makeId("Top.planeOp"),FACE);
            var sketch = newSketch(context, id + "F29", { "sketchPlane" : qUnion([Q0])});
            skPoint(sketch, "E224.0", {"position": v(-222.25, 239.8) * mm});
            skPoint(sketch, "E224.1", {"position": v(101.6, 239.8) * mm});
            skLineSegment(sketch, "E225.bottom", {"start": v(-222.25, 299.53) * mm, "end": v(101.6, 299.53) * mm});
            skLineSegment(sketch, "E225.top", {"start": v(-222.25, 318.58) * mm, "end": v(101.6, 318.58) * mm});
            skLineSegment(sketch, "E225.left", {"start": v(-222.25, 299.53) * mm, "end": v(-222.25, 318.58) * mm});
            skLineSegment(sketch, "E225.right", {"start": v(101.6, 299.53) * mm, "end": v(101.6, 318.58) * mm});
            skLineSegment(sketch, "E226.bottom", {"start": v(-225.43, 321.12) * mm, "end": v(104.77, 321.12) * mm});
            skLineSegment(sketch, "E226.top", {"start": v(-225.43, 305.88) * mm, "end": v(104.77, 305.88) * mm});
            skLineSegment(sketch, "E226.left", {"start": v(-225.43, 321.12) * mm, "end": v(-225.43, 305.88) * mm});
            skLineSegment(sketch, "E226.right", {"start": v(104.77, 321.12) * mm, "end": v(104.77, 305.88) * mm});
            skSolve(sketch);
        }
        {
            var Q0;
            {var subQ0=sQuery(id+"F29.wireOp",EDGE,"E225.bottom");Q0=makeQuery(id+"F29.imprint","IMPRINT",FACE,{"disambiguationData":[TD([[makeQuery(id+"F29.imprint","IMPRINT",EDGE,{"derivedFrom":subQ0}),1.0]])]});}
            extrude(context, id + "F30", {"entities" : qUnion([Q0]), "depth" : 19.05 * mm, "offsetDistance" : 25.4 * mm});
        }
        {
            var Q0;
            {var subQ0=sQuery(id+"F29.wireOp",EDGE,"E225.top");Q0=makeQuery(id+"F29.imprint","IMPRINT",FACE,{"disambiguationData":[TD([[makeQuery(id+"F29.imprint","IMPRINT",EDGE,{"derivedFrom":subQ0}),-1.0]])]});}
            extrude(context, id + "F31", {"entities" : qUnion([Q0]), "operationType" : NewBodyOperationType.ADD, "depth" : 6.35 * mm, "offsetDistance" : 25.4 * mm});
        }
    });
